# Revit family: IS_TonicII_Multiproduct_BIM_GB_R4301;R4302;R4303;R4304
name_source: partatom
category: Plumbing Fixtures
revit_build: Autodesk Revit MEP 2014 (Build: 20140709_2115(x64)
units: mm (PartAtom-declared; Revit-internal decimal feet)

## types (20) — shared parameters
Accessories = www.idealspec.co.uk
AreaUnits = millimeters
Assembly Code = C1030200
AssetType = Fixed
BREEAM = No
Brand = Ideal Standard
Category = Furniture
CodePerformance = EN 14749:2005
ConnectionType = Plumbing
Default Elevation = 800 mm  [stored 2.62467 ft]
DurationUnit = year
ECA = No
ExpectedLife = 30
HandleMatl = ISI_IdealStandard_Handle_Silver_Render
IfcExportAs = IfcFurnitureType
IfcExportType = USERDEFINED
InstallationInstructions = www.idealspec.co.uk/resources.html
LinearUnits = millimeters
Manufacturer = Ideal Standard (UK) Ltd
ManufacturerURL = www.idealspec.co.uk
NBSDescription = Bathroom integrated duct work
NBSReference = 45-35-72/320
NominalHeight = 360 mm  [stored 1.1811 ft]
Shape = Rectangular
Space = Internal
SpareParts = www.fastpart-spares.co.uk
TMV3 = No
URL = www.idealspec.co.uk
Uniclass2015Description = Bathroom integrated duct work
Uniclass2015Reference = Pr_40_30_78_04
Uniclass2015Version = Products v1.1
Version = 1
VolumeUnits = Litres
WRAS = No
WarrantyDescription = Manufacturers Warranty
WarrantyDurationParts = 5
WarrantyDurationUnit = year
WaterEfficientProduct = No
zero-valued in all types: CWFU, Cost, HWFU

## per-type parameters (varying)
| type | BIMObjectName | BarCode | Color | Description | Features | Finish | LaminateFinish | Model | ModelNumber | ModelReference | Name | NettWeight | NominalDepth | NominalLength | NominalWidth | ProductInformation | Size |
| R4301WG - Tonic II 500mm Wall Hung Washbasin Unit - Gloss White | ISI_IdealStandard_Furniture_TonicII_R4301WG | 3391500571501 | Gloss White | Tonic II 500mm wall hung washbasin unit with 1 drawer | 500mm wall hung washbasin unit with 1 drawer | Gloss White | ISI_IdealStandard_Furniture_WhiteWG_Render | R4301WG | R4301WG | Tonic II 500mm wall hung washbasin unit with 1 drawer | ISI_Furniture_TonicII_R4301WG_IdealStandard | 12 Kg | 350 mm | 350 mm | 500 mm | www.idealspec.co.uk/datasheets/R4301WG | 360 x 350 x 500 mm |
| R4303WG - Tonic II 800mm Wall Hung Washbasin Unit - Gloss White | ISI_IdealStandard_Furniture_TonicII_R4303WG | 3391500571600 | Gloss White | Tonic II 800mm wall hung washbasin unit with 1 drawer | 800mm wall hung washbasin unit with 1 drawer | Gloss White | ISI_IdealStandard_Furniture_WhiteWG_Render | R4303WG | R4303WG | Tonic II 800mm wall hung washbasin unit with 1 drawer | ISI_Furniture_TonicII_R4303WG_IdealStandard | 18 Kg | 440 mm  [stored 1.44357 ft] | 440 mm  [stored 1.44357 ft] | 800 mm  [stored 2.62467 ft] | www.idealspec.co.uk/datasheets/R4303WG | 360 x 440 x 800 mm |
| R4304WG - Tonic II 1000mm Wall Hung Washbasin Unit - Gloss White | ISI_IdealStandard_Furniture_TonicII_R4304WG | 3391500571655 | Gloss White | Tonic II 1000mm wall hung washbasin unit with 1 drawer | 1000mm wall hung washbasin unit with 1 drawer | Gloss White | ISI_IdealStandard_Furniture_WhiteWG_Render | R4304WG | R4304WG | Tonic II 1000mm wall hung washbasin unit with 1 drawer | ISI_Furniture_TonicII_R4304WG_IdealStandard | 22 Kg | 440 mm  [stored 1.44357 ft] | 440 mm  [stored 1.44357 ft] | 1000 mm  [stored 3.28084 ft] | www.idealspec.co.uk/datasheets/R4304WG | 360 x 440 x 1000 mm |
| R4301FF - Tonic II 500mm Wall Hung Washbasin Unit - Wood Light Brown | ISI_IdealStandard_Furniture_TonicII_R4301FF | 3391500571532 | Light Brown Wood | Tonic II 500mm wall hung washbasin unit with 1 drawer | 500mm wall hung washbasin unit with 1 drawer | Light Brown Wood | ISI_IdealStandard_Furniture_WoodLightBrownFF_Render | R4301FF | R4301FF | Tonic II 500mm wall hung washbasin unit with 1 drawer | ISI_Furniture_TonicII_R4301FF_IdealStandard | 12 Kg | 350 mm | 350 mm | 500 mm | www.idealspec.co.uk/datasheets/R4301FF | 360 x 350 x 500 mm |
| R4301FE - Tonic II 500mm Wall Hung Washbasin Unit - Wood Light Grey | ISI_IdealStandard_Furniture_TonicII_R4301FE | 3391500571549 | Light Grey Wood | Tonic II 500mm wall hung washbasin unit with 1 drawer | 500mm wall hung washbasin unit with 1 drawer | Light Grey Wood | ISI_IdealStandard_Furniture_WoodLighGreyFE_Render | R4301FE | R4301FE | Tonic II 500mm wall hung washbasin unit with 1 drawer | ISI_Furniture_TonicII_R4301FE_IdealStandard | 12 Kg | 360 mm  [stored 1.1811 ft] | 360 mm  [stored 1.1811 ft] | 500 mm | www.idealspec.co.uk/datasheets/R4301FE | 360 x 360 x 500 mm |
| R4301FA - Tonic II 500mm Wall Hung Washbasin Unit - Gloss Light Grey | ISI_IdealStandard_Furniture_TonicII_R4301FA | 3391500571518 | Light Grey Gloss | Tonic II 500mm wall hung washbasin unit with 1 drawer | 500mm wall hung washbasin unit with 1 drawer | Light Grey Gloss | ISI_IdealStandard_Furniture_GlossLightGreyFA_Render | R4301FA | R4301FA | Tonic II 500mm wall hung washbasin unit with 1 drawer | ISI_Furniture_TonicII_R4301FA_IdealStandard | 12 Kg | 350 mm | 350 mm | 500 mm | www.idealspec.co.uk/datasheets/R4301FA | 360 x 350 x 500 mm |
| R4301FC - Tonic II 500mm Wall Hung Washbasin Unit - GLoss Light Brown | ISI_IdealStandard_Furniture_TonicII_R4301FC | 3391500571525 | Light Brown Gloss | Tonic II 500mm wall hung washbasin unit with 1 drawer | 500mm wall hung washbasin unit with 1 drawer | Light Brown Gloss | ISI_IdealStandard_Furniture_GlossLightBrownFC_Render | R4301FC | R4301FC | Tonic II 500mm wall hung washbasin unit with 1 drawer | ISI_Furniture_TonicII_R4301FC_IdealStandard | 12 Kg | 350 mm | 350 mm | 500 mm | www.idealspec.co.uk/datasheets/R4301FC | 360 x 350 x 500 mm |
| R4302WG - Tonic II 600mm Wall Hung Washbasin Unit - Gloss White | ISI_IdealStandard_Furniture_TonicII_R4302WG | 3391500571556 | Gloss White | Tonic II 600mm wall hung washbasin unit with 1 drawer | 600mm wall hung washbasin unit with 1 drawer | Gloss White | ISI_IdealStandard_Furniture_WhiteWG_Render | R4302WG | R4302WG | Tonic II 600mm wall hung washbasin unit with 1 drawer | ISI_Furniture_TonicII_R4302WG_IdealStandard | 15 Kg | 440 mm  [stored 1.44357 ft] | 440 mm  [stored 1.44357 ft] | 600 mm | www.idealspec.co.uk/datasheets/R4302WG | 360 x 440 x 600 mm |
| R4302FC - Tonic II 600mm Wall Hung Washbasin Unit - Gloss Light Brown | ISI_IdealStandard_Furniture_TonicII_R4302FC | 3391500571570 | Light Brown Gloss | Tonic II 600mm wall hung washbasin unit with 1 drawer | 600mm wall hung washbasin unit with 1 drawer | Light Brown Gloss | ISI_IdealStandard_Furniture_GlossLightBrownFC_Render | R4302FC | R4302FC | Tonic II 600mm wall hung washbasin unit with 1 drawer | ISI_Furniture_TonicII_R4302FC_IdealStandard | 15 Kg | 440 mm  [stored 1.44357 ft] | 440 mm  [stored 1.44357 ft] | 600 mm | www.idealspec.co.uk/datasheets/R4302FC | 360 x 440 x 600 mm |
| R4302FA - Tonic II 600mm Wall Hung Washbasin Unit - Gloss Light Grey | ISI_IdealStandard_Furniture_TonicII_R4302FA | 3391500571563 | Light Grey Gloss | Tonic II 600mm wall hung washbasin unit with 1 drawer | 600mm wall hung washbasin unit with 1 drawer | Light Grey Gloss | ISI_IdealStandard_Furniture_GlossLightGreyFA_Render | R4302FA | R4302FA | Tonic II 600mm wall hung washbasin unit with 1 drawer | ISI_Furniture_TonicII_R4302FA_IdealStandard | 15 Kg | 440 mm  [stored 1.44357 ft] | 440 mm  [stored 1.44357 ft] | 600 mm | www.idealspec.co.uk/datasheets/R4302FA | 360 x 440 x 600 mm |
| R4302FF - Tonic II 600mm Wall Hung Washbasin Unit - Wood Light Brown | ISI_IdealStandard_Furniture_TonicII_R4302FF | 3391500571587 | Light Brown Wood | Tonic II 600mm wall hung washbasin unit with 1 drawer | 600mm wall hung washbasin unit with 1 drawer | Light Brown Wood | ISI_IdealStandard_Furniture_WoodLightBrownFF_Render | R4302FF | R4302FF | Tonic II 600mm wall hung washbasin unit with 1 drawer | ISI_Furniture_TonicII_R4302FF_IdealStandard | 15 Kg | 440 mm  [stored 1.44357 ft] | 440 mm  [stored 1.44357 ft] | 600 mm | www.idealspec.co.uk/datasheets/R4302FF | 360 x 440 x 600 mm |
| R4302FE - Tonic II 600mm Wall Hung Washbasin Unit - Wood Light Grey | ISI_IdealStandard_Furniture_TonicII_R4302FE | 3391500571594 | Light Grey Wood | Tonic II 600mm wall hung washbasin unit with 1 drawer | 600mm wall hung washbasin unit with 1 drawer | Light Grey Wood | ISI_IdealStandard_Furniture_WoodLighGreyFE_Render | R4302FE | R4302FE | Tonic II 600mm wall hung washbasin unit with 1 drawer | ISI_Furniture_TonicII_R4302FE_IdealStandard | 15 Kg | 440 mm  [stored 1.44357 ft] | 440 mm  [stored 1.44357 ft] | 600 mm | www.idealspec.co.uk/datasheets/R4302FE | 360 x 440 x 600 mm |
| R4303FC - Tonic II 800mm Wall Hung Washbasin Unit - Gloss Light Brown | ISI_IdealStandard_Furniture_TonicII_R4303FC | 3391500571624 | Light Brown Gloss | Tonic II 800mm wall hung washbasin unit with 1 drawer | 800mm wall hung washbasin unit with 1 drawer | Light Brown Gloss | ISI_IdealStandard_Furniture_GlossLightBrownFC_Render | R4303FC | R4303FC | Tonic II 800mm wall hung washbasin unit with 1 drawer | ISI_Furniture_TonicII_R4303FC_IdealStandard | 18 Kg | 440 mm  [stored 1.44357 ft] | 440 mm  [stored 1.44357 ft] | 800 mm  [stored 2.62467 ft] | www.idealspec.co.uk/datasheets/R4303FC | 360 x 440 x 800 mm |
| R4303FA - Tonic II 800mm Wall Hung Washbasin Unit - Gloss Light Grey | ISI_IdealStandard_Furniture_TonicII_R4303FA | 3391500571617 | Light Grey Gloss | Tonic II 800mm wall hung washbasin unit with 1 drawer | 800mm wall hung washbasin unit with 1 drawer | Light Grey Gloss | ISI_IdealStandard_Furniture_GlossLightGreyFA_Render | R4303FA | R4303FA | Tonic II 800mm wall hung washbasin unit with 1 drawer | ISI_Furniture_TonicII_R4303FA_IdealStandard | 18 Kg | 440 mm  [stored 1.44357 ft] | 440 mm  [stored 1.44357 ft] | 800 mm  [stored 2.62467 ft] | www.idealspec.co.uk/datasheets/R4303FA | 360 x 440 x 800 mm |
| R4303FF - Tonic II 800mm Wall Hung Washbasin Unit - Wood Light Brown | ISI_IdealStandard_Furniture_TonicII_R4303FF | 3391500571631 | Light Brown Wood | Tonic II 800mm wall hung washbasin unit with 1 drawer | 800mm wall hung washbasin unit with 1 drawer | Light Brown Wood | ISI_IdealStandard_Furniture_WoodLightBrownFF_Render | R4303FF | R4303FF | Tonic II 800mm wall hung washbasin unit with 1 drawer | ISI_Furniture_TonicII_R4303FF_IdealStandard | 18 Kg | 440 mm  [stored 1.44357 ft] | 440 mm  [stored 1.44357 ft] | 800 mm  [stored 2.62467 ft] | www.idealspec.co.uk/datasheets/R4303FF | 360 x 440 x 800 mm |
| R4303FE - Tonic II 800mm Wall Hung Washbasin Unit - Wood Light Gery | ISI_IdealStandard_Furniture_TonicII_R4303FE | 3391500571648 | Light Grey Wood | Tonic II 800mm wall hung washbasin unit with 1 drawer | 800mm wall hung washbasin unit with 1 drawer | Light Grey Wood | ISI_IdealStandard_Furniture_WoodLighGreyFE_Render | R4303FE | R4303FE | Tonic II 800mm wall hung washbasin unit with 1 drawer | ISI_Furniture_TonicII_R4303FE_IdealStandard | 18 Kg | 440 mm  [stored 1.44357 ft] | 440 mm  [stored 1.44357 ft] | 800 mm  [stored 2.62467 ft] | www.idealspec.co.uk/datasheets/R4303FE | 360 x 440 x 800 mm |
| R4304FC - Tonic II 1000mm Wall Hung Washbasin Unit - Gloss Light Brown | ISI_IdealStandard_Furniture_TonicII_R4304FC | 3391500571679 | Light Brown Gloss | Tonic II 1000mm wall hung washbasin unit with 1 drawer | 1000mm wall hung washbasin unit with 1 drawer | Light Brown Gloss | ISI_IdealStandard_Furniture_GlossLightBrownFC_Render | R4304FC | R4304FC | Tonic II 1000mm wall hung washbasin unit with 1 drawer | ISI_Furniture_TonicII_R4304FC_IdealStandard | 22 Kg | 440 mm  [stored 1.44357 ft] | 440 mm  [stored 1.44357 ft] | 1000 mm  [stored 3.28084 ft] | www.idealspec.co.uk/datasheets/R4304FC | 360 x 440 x 1000 mm |
| R4304FA - Tonic II 1000mm Wall Hung Washbasin Unit - Gloss Light Grey | ISI_IdealStandard_Furniture_TonicII_R4304FA | 3391500571662 | Light Grey Gloss | Tonic II 1000mm wall hung washbasin unit with 1 drawer | 1000mm wall hung washbasin unit with 1 drawer | Light Grey Gloss | ISI_IdealStandard_Furniture_GlossLightGreyFA_Render | R4304FA | R4304FA | Tonic II 1000mm wall hung washbasin unit with 1 drawer | ISI_Furniture_TonicII_R4304FA_IdealStandard | 22 Kg | 440 mm  [stored 1.44357 ft] | 440 mm  [stored 1.44357 ft] | 1000 mm  [stored 3.28084 ft] | www.idealspec.co.uk/datasheets/R4304FA | 360 x 440 x 1000 mm |
| R4304FF - Tonic II 1000mm Wall Hung Washbasin Unit - Wood Light Brown | ISI_IdealStandard_Furniture_TonicII_R4304FF | 3391500571686 | Light Brown Wood | Tonic II 1000mm wall hung washbasin unit with 1 drawer | 1000mm wall hung washbasin unit with 1 drawer | Light Brown Wood | ISI_IdealStandard_Furniture_WoodLightBrownFF_Render | R4304FF | R4304FF | Tonic II 1000mm wall hung washbasin unit with 1 drawer | ISI_Furniture_TonicII_R4304FF_IdealStandard | 22 Kg | 440 mm  [stored 1.44357 ft] | 440 mm  [stored 1.44357 ft] | 1000 mm  [stored 3.28084 ft] | www.idealspec.co.uk/datasheets/R4304FF | 360 x 440 x 1000 mm |
| R4304FE - Tonic II 1000mm Wall Hung Washbasin Unit - Wood Light Grey | ISI_IdealStandard_Furniture_TonicII_R4304FE | 3391500571693 | Light Grey Wood | Tonic II 1000mm wall hung washbasin unit with 1 drawer | 1000mm wall hung washbasin unit with 1 drawer | Light Grey Wood | ISI_IdealStandard_Furniture_WoodLighGreyFE_Render | R4304FE | R4304FE | Tonic II 1000mm wall hung washbasin unit with 1 drawer | ISI_Furniture_TonicII_R4304FE_IdealStandard | 22 Kg | 440 mm  [stored 1.44357 ft] | 440 mm  [stored 1.44357 ft] | 1000 mm  [stored 3.28084 ft] | www.idealspec.co.uk/datasheets/R4304FE | 360 x 440 x 1000 mm |

note: [stored X ft] marks values corroborated as IEEE doubles in the binary element streams (Revit-internal decimal feet)

## geometry (parser evidence)
native form markers: Sweep x5
no freeform markers — native parametric forms only
